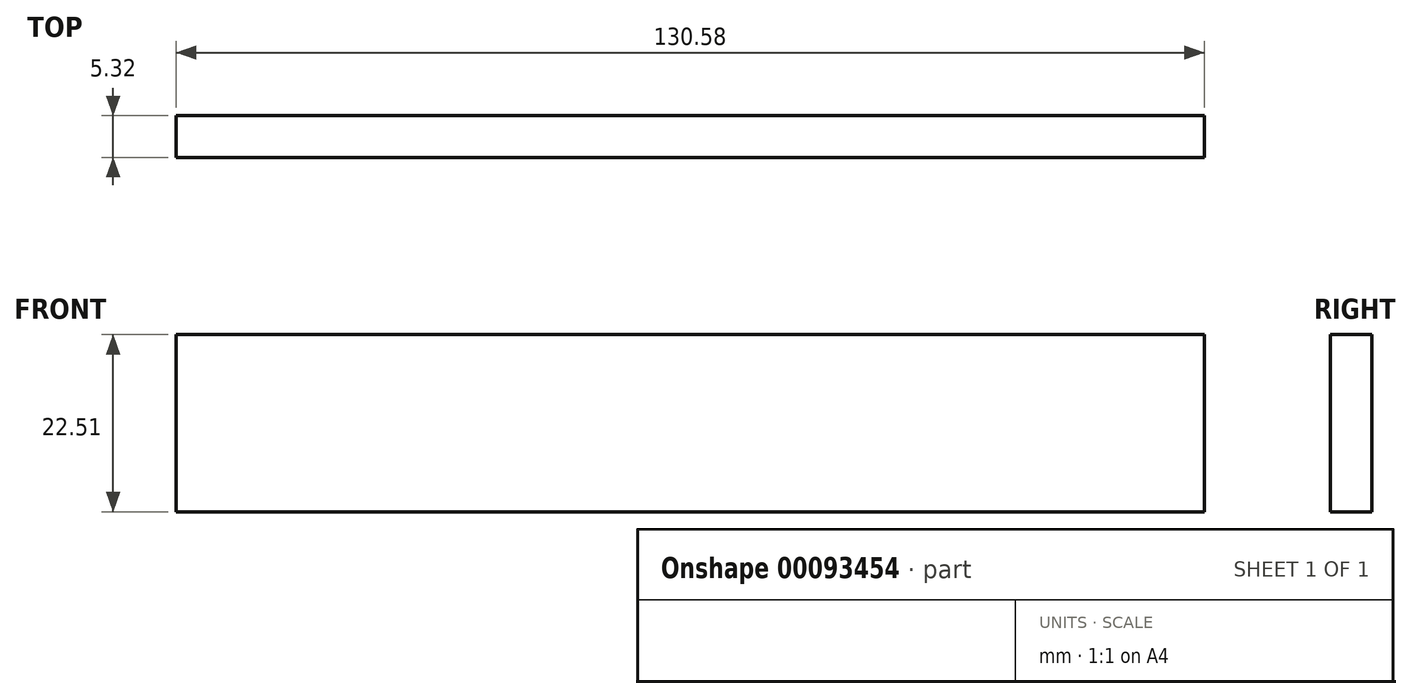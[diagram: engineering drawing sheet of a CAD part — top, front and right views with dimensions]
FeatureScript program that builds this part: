
annotation { "Feature Type Name" : "Feature", "Feature Type Description" : "" }
export const myFeature = defineFeature(function(context is Context, id is Id, definition is map)
    precondition{}
    {
        {
            var Q0;
            Q0=qCreatedBy(makeId("Front.planeOp"),FACE);
            var sketch = newSketch(context, id + "F0", { "sketchPlane" : qUnion([Q0])});
            skLineSegment(sketch, "E0.bottom", {"start": v(-61.3, 60.61) * mm, "end": v(69.27, 60.61) * mm});
            skLineSegment(sketch, "E0.top", {"start": v(-61.3, 38.1) * mm, "end": v(69.27, 38.1) * mm});
            skLineSegment(sketch, "E0.left", {"start": v(-61.3, 60.61) * mm, "end": v(-61.3, 38.1) * mm});
            skLineSegment(sketch, "E0.right", {"start": v(69.27, 60.61) * mm, "end": v(69.27, 38.1) * mm});
            skSolve(sketch);
        }
        {
            var Q0;
            Q0=makeQuery(id+"F0.imprint","IMPRINT",FACE,{"disambiguationData":[TD([[makeQuery(id+"F0.imprint","IMPRINT",EDGE,{"derivedFrom":sQuery(id+"F0.wireOp",EDGE,"E0.bottom")}),-1.0]])]});
            extrude(context, id + "F1", {"entities" : qUnion([Q0]), "depth" : 5.32 * mm});
        }
    });
